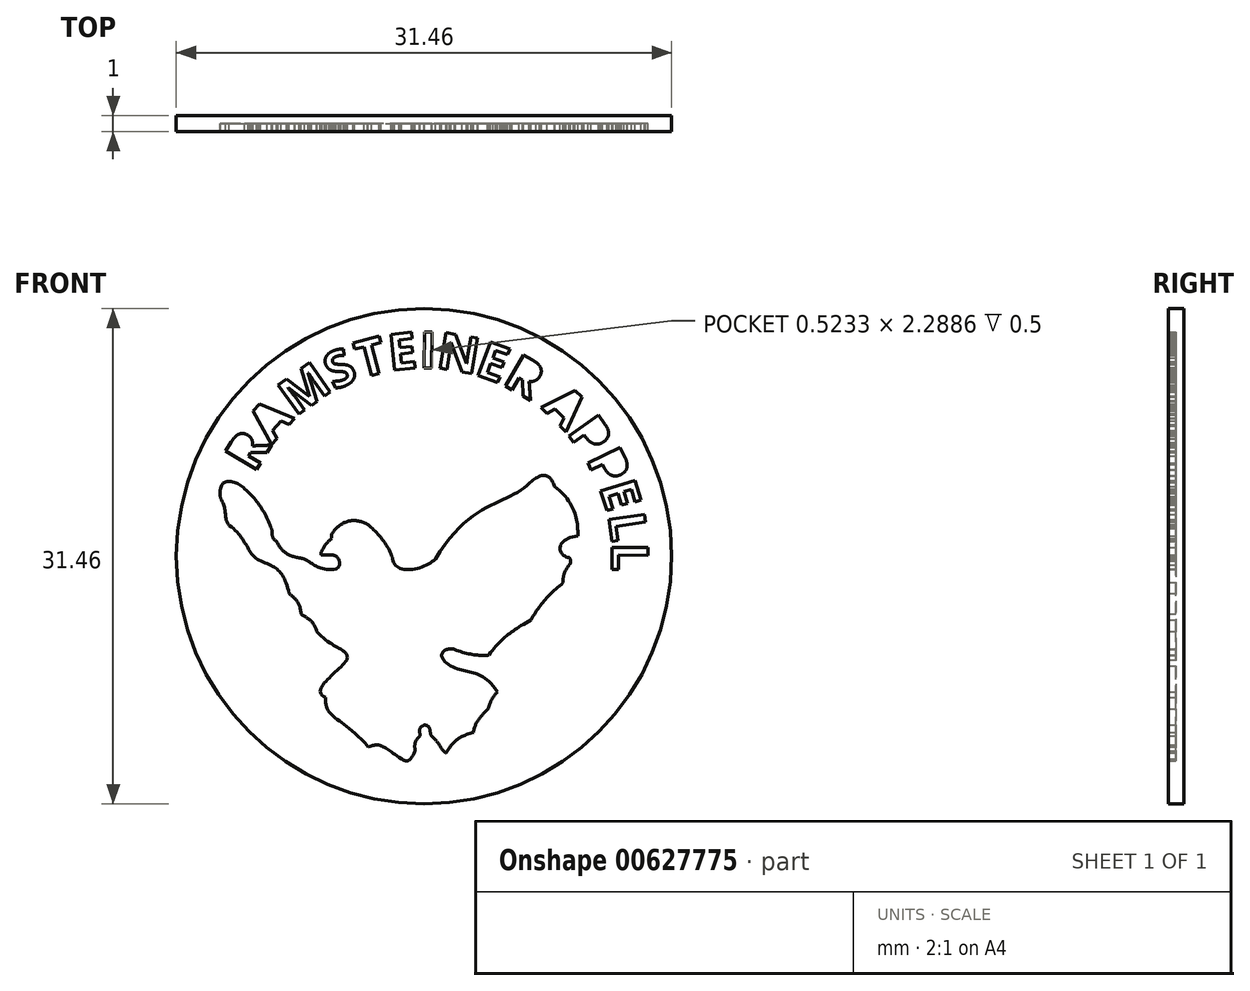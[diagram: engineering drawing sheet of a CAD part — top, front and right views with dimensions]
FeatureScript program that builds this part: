
annotation { "Feature Type Name" : "Feature", "Feature Type Description" : "" }
export const myFeature = defineFeature(function(context is Context, id is Id, definition is map)
    precondition{}
    {
        {
            var Q0;
            Q0=qCreatedBy(makeId("Front.planeOp"),FACE);
            var sketch = newSketch(context, id + "F0", { "sketchPlane" : qUnion([Q0])});
            skSolve(sketch);
        }
        {
            var Q0;
            Q0=qCreatedBy(makeId("Front.planeOp"),FACE);
            var sketch = newSketch(context, id + "F1", { "sketchPlane" : qUnion([Q0])});
            skFitSpline(sketch, "E0", {"points": [v(17.65, 7.14) * mm, v(17.38, 6.45) * mm], "startDerivative": vector(-1.2, -0.3) * mm, "endDerivative": vector(0.13, -0.84) * mm});
            skFitSpline(sketch, "E1", {"points": [v(17.38, 6.45) * mm, v(17.07, 5.5) * mm], "startDerivative": vector(-1.26, -0.95) * mm, "endDerivative": vector(0.15, -0.8) * mm});
            skFitSpline(sketch, "E2", {"points": [v(17.07, 5.5) * mm, v(16.2, 4.98) * mm], "startDerivative": vector(-0.96, -1.8) * mm, "endDerivative": vector(-1.3, 0.83) * mm});
            skFitSpline(sketch, "E3", {"points": [v(16.2, 4.98) * mm, v(14.08, 5.76) * mm], "startDerivative": vector(-3.55, 2.4) * mm, "endDerivative": vector(-2.39, -0.94) * mm});
            skFitSpline(sketch, "E4", {"points": [v(14.08, 5.76) * mm, v(11.38, 8.9) * mm], "startDerivative": vector(-5.17, 5.95) * mm, "endDerivative": vector(0.3, 4.18) * mm});
            skFitSpline(sketch, "E5", {"points": [v(11.38, 8.9) * mm, v(12.72, 11.28) * mm], "startDerivative": vector(-3.38, 1.37) * mm, "endDerivative": vector(1.49, 2.32) * mm});
            skFitSpline(sketch, "E6", {"points": [v(12.72, 11.28) * mm, v(10.81, 13.08) * mm], "startDerivative": vector(0.67, 2.04) * mm, "endDerivative": vector(-3.34, 3.57) * mm});
            skFitSpline(sketch, "E7", {"points": [v(10.81, 13.08) * mm, v(9.8, 14.19) * mm], "startDerivative": vector(-0.47, 1.94) * mm, "endDerivative": vector(-1.57, 0.97) * mm});
            skFitSpline(sketch, "E8", {"points": [v(9.8, 14.19) * mm, v(9.05, 15.5) * mm], "startDerivative": vector(-0.03, 2.36) * mm, "endDerivative": vector(-1.02, 0.8) * mm});
            skFitSpline(sketch, "E9", {"points": [v(9.05, 15.5) * mm, v(7.13, 17.63) * mm], "startDerivative": vector(-1.01, 4.46) * mm, "endDerivative": vector(-3.5, 1.44) * mm});
            skFitSpline(sketch, "E10", {"points": [v(7.13, 17.63) * mm, v(5.26, 19.83) * mm], "startDerivative": vector(-2.03, 0.95) * mm, "endDerivative": vector(-3.23, 2.3) * mm});
            skFitSpline(sketch, "E11", {"points": [v(5.26, 19.83) * mm, v(4.7, 21.54) * mm], "startDerivative": vector(-1.22, 1.05) * mm, "endDerivative": vector(-1.53, 2.36) * mm});
            skFitSpline(sketch, "E12", {"points": [v(4.7, 21.54) * mm, v(6.24, 22.14) * mm], "startDerivative": vector(-0.66, 4.43) * mm, "endDerivative": vector(1.87, -1.82) * mm});
            skFitSpline(sketch, "E13", {"points": [v(6.24, 22.14) * mm, v(7.93, 19.63) * mm], "startDerivative": vector(2.43, -2.04) * mm, "endDerivative": vector(0.92, -2.6) * mm});
            skFitSpline(sketch, "E14", {"points": [v(7.93, 19.63) * mm, v(8.26, 18.8) * mm], "startDerivative": vector(0.35, -0.59) * mm, "endDerivative": vector(1.38, -1.11) * mm});
            skFitSpline(sketch, "E15", {"points": [v(8.26, 18.8) * mm, v(9.78, 17.75) * mm], "startDerivative": vector(1.1, -2.15) * mm, "endDerivative": vector(2.13, -0.3) * mm});
            skFitSpline(sketch, "E16", {"points": [v(9.78, 17.75) * mm, v(12.04, 17.06) * mm], "startDerivative": vector(1.74, -0.1) * mm, "endDerivative": vector(4, 0.58) * mm});
            skFitSpline(sketch, "E17", {"points": [v(12.04, 17.06) * mm, v(11.77, 17.94) * mm], "startDerivative": vector(1.17, 0.39) * mm, "endDerivative": vector(-1.57, 0) * mm});
            skLineSegment(sketch, "E18", {"start": v(11.77, 17.94) * mm, "end": v(11.14, 17.94) * mm});
            skFitSpline(sketch, "E19", {"points": [v(11.14, 17.94) * mm, v(11.77, 18.98) * mm], "startDerivative": vector(-0.65, 0.03) * mm, "endDerivative": vector(1.27, 0.76) * mm});
            skFitSpline(sketch, "E20", {"points": [v(11.77, 18.98) * mm, v(12.37, 19.9) * mm], "startDerivative": vector(-0.47, 0.74) * mm, "endDerivative": vector(1.03, 0.57) * mm});
            skFitSpline(sketch, "E21", {"points": [v(12.37, 19.9) * mm, v(14.03, 19.9) * mm], "startDerivative": vector(1.43, 0.9) * mm, "endDerivative": vector(2.02, -1.05) * mm});
            skEllipse(sketch, "E22", {"center": v(12.6, 19.18) * mm, "majorRadius": 0.28 * mm, "minorRadius": 0.18 * mm, "majorAxis": v(0.53, -0.85)});
            skFitSpline(sketch, "E23", {"points": [v(14.03, 19.9) * mm, v(15.65, 17.58) * mm], "startDerivative": vector(1.6, -1.12) * mm, "endDerivative": vector(0.23, -2.3) * mm});
            skFitSpline(sketch, "E24", {"points": [v(15.65, 17.58) * mm, v(18.35, 17.7) * mm], "startDerivative": vector(0.7, -2.75) * mm, "endDerivative": vector(2.07, 2.14) * mm});
            skFitSpline(sketch, "E25", {"points": [v(18.35, 17.7) * mm, v(24.35, 22.54) * mm], "startDerivative": vector(6.94, 11.52) * mm, "endDerivative": vector(4, 4.33) * mm});
            skFitSpline(sketch, "E26", {"points": [v(24.35, 22.54) * mm, v(25.91, 22.3) * mm], "startDerivative": vector(2.4, 2.01) * mm, "endDerivative": vector(0.87, -2.64) * mm});
            skFitSpline(sketch, "E27", {"points": [v(25.91, 22.3) * mm, v(27.4, 19.16) * mm], "startDerivative": vector(3.78, -2.96) * mm, "endDerivative": vector(0.04, -3.53) * mm});
            skFitSpline(sketch, "E28", {"points": [v(27.4, 19.16) * mm, v(26.85, 17.77) * mm], "startDerivative": vector(-4.4, -0.49) * mm, "endDerivative": vector(2.44, -0.48) * mm});
            skFitSpline(sketch, "E29", {"points": [v(26.85, 17.77) * mm, v(26.85, 17.32) * mm], "startDerivative": vector(0.22, -0.09) * mm, "endDerivative": vector(-0.4, -0.42) * mm});
            skFitSpline(sketch, "E30", {"points": [v(26.85, 17.32) * mm, v(26.47, 16.19) * mm], "startDerivative": vector(-1.02, -1.11) * mm, "endDerivative": vector(0.16, -0.79) * mm});
            skFitSpline(sketch, "E31", {"points": [v(26.47, 16.19) * mm, v(24.41, 13.82) * mm], "startDerivative": vector(-2.89, -2.4) * mm, "endDerivative": vector(-1.7, -2.94) * mm});
            skFitSpline(sketch, "E32", {"points": [v(24.41, 13.82) * mm, v(21.75, 11.6) * mm], "startDerivative": vector(-3.92, -2.26) * mm, "endDerivative": vector(-2.6, -3.42) * mm});
            skFitSpline(sketch, "E33", {"points": [v(21.75, 11.6) * mm, v(19.57, 11.95) * mm], "startDerivative": vector(-0.3, -0.3) * mm, "endDerivative": vector(-2.75, 1.2) * mm});
            skFitSpline(sketch, "E34", {"points": [v(19.57, 11.95) * mm, v(19.31, 10.91) * mm], "startDerivative": vector(-1.72, 0.61) * mm, "endDerivative": vector(3.4, -2) * mm});
            skFitSpline(sketch, "E35", {"points": [v(19.31, 10.91) * mm, v(22.3, 9.26) * mm], "startDerivative": vector(3.53, -1.86) * mm, "endDerivative": vector(3.33, -4.7) * mm});
            skFitSpline(sketch, "E36", {"points": [v(22.3, 9.26) * mm, v(21.7, 8.16) * mm], "startDerivative": vector(-1.03, -1.03) * mm, "endDerivative": vector(-0.37, -1.24) * mm});
            skFitSpline(sketch, "E37", {"points": [v(21.7, 8.16) * mm, v(20.77, 6.69) * mm], "startDerivative": vector(-1.58, -1.53) * mm, "endDerivative": vector(-0.26, -1.79) * mm});
            skFitSpline(sketch, "E38", {"points": [v(20.77, 6.69) * mm, v(19.03, 5.38) * mm], "startDerivative": vector(-2.88, -0.88) * mm, "endDerivative": vector(-1.43, -2.34) * mm});
            skFitSpline(sketch, "E39", {"points": [v(19.03, 5.38) * mm, v(18.09, 6.45) * mm], "startDerivative": vector(-0.94, 0.27) * mm, "endDerivative": vector(-1.75, 1.34) * mm});
            skFitSpline(sketch, "E40", {"points": [v(18.09, 6.45) * mm, v(17.65, 7.14) * mm], "startDerivative": vector(-0.37, 0.67) * mm, "endDerivative": vector(-1.32, -0.1) * mm});
            skCircle(sketch, "E41", {"center": v(17.62, 17.87) * mm, "radius": 15.73 * mm});
            skText(sketch, "E42", { "text": "R", "fontName": "OpenSans-Bold.ttf"});
            skText(sketch, "E43", { "text": "A", "fontName": "OpenSans-Bold.ttf"});
            skText(sketch, "E44", { "text": "M", "fontName": "OpenSans-Bold.ttf"});
            skText(sketch, "E45", { "text": "S", "fontName": "OpenSans-Bold.ttf"});
            skCircle(sketch, "E46", {"center": v(17.62, 17.87) * mm, "radius": 11.95 * mm, "construction": true});
            skText(sketch, "E47", { "text": "T", "fontName": "OpenSans-Bold.ttf"});
            skText(sketch, "E48", { "text": "E", "fontName": "OpenSans-Bold.ttf"});
            skText(sketch, "E49", { "text": "I", "fontName": "OpenSans-Bold.ttf"});
            skText(sketch, "E50", { "text": "N", "fontName": "OpenSans-Bold.ttf"});
            skText(sketch, "E51", { "text": "E", "fontName": "OpenSans-Bold.ttf"});
            skText(sketch, "E52", { "text": "R", "fontName": "OpenSans-Bold.ttf"});
            skText(sketch, "E53", { "text": "A", "fontName": "OpenSans-Bold.ttf"});
            skText(sketch, "E54", { "text": "P", "fontName": "OpenSans-Bold.ttf"});
            skText(sketch, "E55", { "text": "P", "fontName": "OpenSans-Bold.ttf"});
            skText(sketch, "E56", { "text": "E", "fontName": "OpenSans-Bold.ttf"});
            skText(sketch, "E57", { "text": "L", "fontName": "OpenSans-Bold.ttf"});
            skText(sketch, "E58", { "text": "L", "fontName": "OpenSans-Bold.ttf"});
            const initialGuessF1  = {"E42": [0.00683, 0.02313, 0.5225, 0.85264, 0.0023], "E43": [0.00794, 0.02497, 0.66913, 0.74314, 0.0023], "E44": [0.00946, 0.02672, 0.81208, 0.58354, 0.0023], "E45": [0.01192, 0.02841, 0.91355, 0.40674, 0.0023], "E47": [0.01363, 0.02918, 0.96727, 0.25376, 0.0023], "E48": [0.01548, 0.02966, 0.99452, 0.10453, 0.0023], "E49": [0.01734, 0.02983, 0.99985, -0.01745, 0.0023], "E50": [0.01837, 0.02986, 0.986, -0.16677, 0.0023], "E51": [0.0208, 0.02943, 0.94147, -0.3371, 0.0023], "E52": [0.02256, 0.02882, 0.86777, -0.49697, 0.0023], "E53": [0.02506, 0.0273, 0.71934, -0.69466, 0.0023], "E54": [0.0279, 0.02404, 0.43837, -0.8988, 0.0023], "E55": [0.02668, 0.02573, 0.58779, -0.80902, 0.0023], "E56": [0.02876, 0.02229, 0.29737, -0.95476, 0.0023], "E57": [0.02932, 0.02048, 0.13917, -0.99027, 0.0023], "E58": [0.02958, 0.01872, -0.00873, -0.99996, 0.0023]};
            skSetInitialGuess(sketch, initialGuessF1);
            skSolve(sketch);
        }
        {
            var Q0;
            Q0 = qSketchRegion(id + "F1", true);
            extrude(context, id + "F2", {"entities" : qUnion([Q0]), "depth" : 1 * mm, "offsetDistance" : 25 * mm});
        }
        {
            var Q0;
            Q0=qCreatedBy(makeId("Front.planeOp"),FACE);
            var sketch = newSketch(context, id + "F3", { "sketchPlane" : qUnion([Q0])});
            skCircle(sketch, "E59.0", {"center": v(17.62, 17.87) * mm, "radius": 15.73 * mm});
            skSolve(sketch);
        }
        {
            var Q0;
            Q0 = qSketchRegion(id + "F3", true);
            extrude(context, id + "F4", {"entities" : qUnion([Q0]), "operationType" : NewBodyOperationType.ADD, "depth" : 0.5 * mm, "offsetDistance" : 25 * mm});
        }
    });
